# Revit family: Drinking_Fountain-Haws_Corporation-Wall_Mounted_1109
name_source: partatom
category: Plumbing Fixtures
units: mm (PartAtom-declared; Revit-internal decimal feet)

## family parameters
Always vertical = Yes
Cut with Voids When Loaded = No
Host = Wall
OmniClass Number = 23.65.70.14.11
Part Type = Normal
Room Calculation Point = No
Round Connector Dimension = Use Radius
Shared = Yes

## types (12) — shared parameters
Apparent Load = 0 VA
Back Panel = Metal - Haws Corporation - Stainless Steel - Satin BP3
Bowl = Metal - Haws Corporation - Stainless Steel - Satin BP3
Bowl Width = 1' - 3"
CW Connection = Yes
Cost = $0
Current = 0 A
Default Elevation = 0' - 0"
Electrical Connection Note = Electrical connection is only required for products that contain touchless sensors
Flow = 0.00 GPM
Manufacturer = Haws Corporation 1455 Kleppe Lane Sparks, NV 89431
Number of Poles = 1
Power Factor = 1
Product Page URL = https://www.hawsco.com
Product data url = https://www.bimobject.com
Sanitary Radius = 0' - 0 5/8"
Trim = Metal - Haws Corporation - Stainless Steel - Satin BP3
Tubing = Metal - Haws Corporation - Copper Poly
URL = http://www.hawsco.com
VC = No
Waste Level = 2' - 7 1/8"
zero-valued in all types: HWFU

## per-type parameters (varying)
| type | 1920FR | 6521FR | BP3 for 6521FR | CWFU | Connector | Connector visibility | Description | HW Connection | Nr | Supply Level | Supply Radius | Touchless Sensor | Trim Plate | Type Comments | Vent Connection | Voltage | WC 1920FR | WC 6521FR | WFU | Waste Connection |
| 1109 | No | No | No | 1 | 3 | Yes | 18 gauge Type 304 Stainless Steel design without back panel | No | 2 | 2' - 4 5/8" | 0' - 0 3/16" | No | No | Placed securely in multiple locations without taking up excess space | Yes | 0 V | 2 | 2 | 0 | No |
| 1109HO | No | No | No | 1 | 3 | Yes | 18 gauge Type 304 Stainless Steel design without back panel | No | 3 | 2' - 4 5/8" | 0' - 0 3/16" | Yes | No | Placed securely in multiple locations without taking up excess space | Yes | 24 V | 2 | 2 | 0 | No |
| 1109.14 | No | No | No | 1 | 3 | Yes | 14 gauge Type 304 Stainless Steel design without back panel | No | 2 | 2' - 4 5/8" | 0' - 0 3/16" | No | No | Placed securely in multiple locations without taking up excess space | Yes | 0 V | 2 | 2 | 0 | No |
| 1109.14HO | No | No | No | 1 | 3 | Yes | 14 gauge Type 304 Stainless Steel design without back panel | No | 3 | 2' - 4 5/8" | 0' - 0 3/16" | Yes | No | Placed securely in multiple locations without taking up excess space | Yes | 24 V | 2 | 2 | 0 | No |
| 1109BP | No | No | No | 1 | 3 | Yes | Design with matching back panel | No | 2 | 2' - 4 5/8" | 0' - 0 3/16" | No | No | Placed securely in multiple locations without taking up excess space | Yes | 0 V | 2 | 2 | 1 | Yes |
| 1109BPHO | No | No | No | 1 | 3 | Yes | Design with matching back panel | No | 3 | 2' - 4 5/8" | 0' - 0 3/16" | Yes | No | Placed securely in multiple locations without taking up excess space | Yes | 24 V | 2 | 2 | 1 | Yes |
| 1109FR | No | No | No | 1 | 3 | Yes | Fountain uses a fully engineered pneumatic operated freeze-resistant valve assembly for continual use during winter months | No | 2 | 2' - 4 5/8" | 0' - 0 3/16" | No | No | Without Back Panel, wall mounted, barrier-free, stainless steel drinking fountain with satin finish | Yes | 0 V | 2 | 2 | 0 | No |
| 1109FRBP | No | No | No | 1 | 3 | Yes | Fountain uses a fully engineered pneumatic operated freeze-resistant valve assembly for continual use during winter months | No | 2 | 2' - 4 5/8" | 0' - 0 3/16" | No | No | Design with matching back panel, wall mounted, barrier-free, stainless steel drinking fountain with satin finish | Yes | 0 V | 2 | 2 | 1 | Yes |
| H1109.8 | No | No | No | 2 | 3 | Yes | Designed to run at a low energy usage, this water cooler and fountain are assured to have a long lasting life | Yes | 2 | 2' - 1 1/8" | 0' - 0 3/16" | No | Yes | Electric drinking fountain provides 8 gph chilled water | No | 0 V | 2 | 2 | 1 | Yes |
| H1109.8HO | No | No | No | 2 | 3 | Yes | Designed to run at a low energy usage, this water cooler and fountain are assured to have a long lasting life | Yes | 3 | 2' - 1 1/8" | 0' - 0 3/16" | Yes | Yes | Electric drinking fountain provides 8 gph chilled water | No | 24 V | 2 | 2 | 1 | Yes |
| 1109FRB | No | Yes | Yes | 1 | 2 | No | Model 1109FRB, Barrier-Free Freeze Resistant Wall Mount Fountain with 6521FR In-Wall Valve | No | 2 | 2' - 4 5/8" | 0' - 0 1/4" | No | No | Without Back Panel, wall mounted, barrier-free, stainless steel drinking fountain with satin finish | Yes | 0 V | 2 | 3 | 0 | No |
| 1109FRP | Yes | Yes | No | 1 | 2 | No | Model 1109FRP, Barrier-Free Freeze Resistant Wall Mount Fountain with 1920FR Bottle Filler and 6521FR In-Wall Valve | No | 2 | 2' - 4 5/8" | 0' - 0 1/4" | No | No | Without Back Panel, wall mounted, barrier-free, stainless steel drinking fountain with satin finish | Yes | 0 V | 3 | 3 | 0 | No |

note: column(s) folded — value = type name in every type: Model

## geometry (parser evidence)
native form markers: Sweep x9
no freeform markers — native parametric forms only
